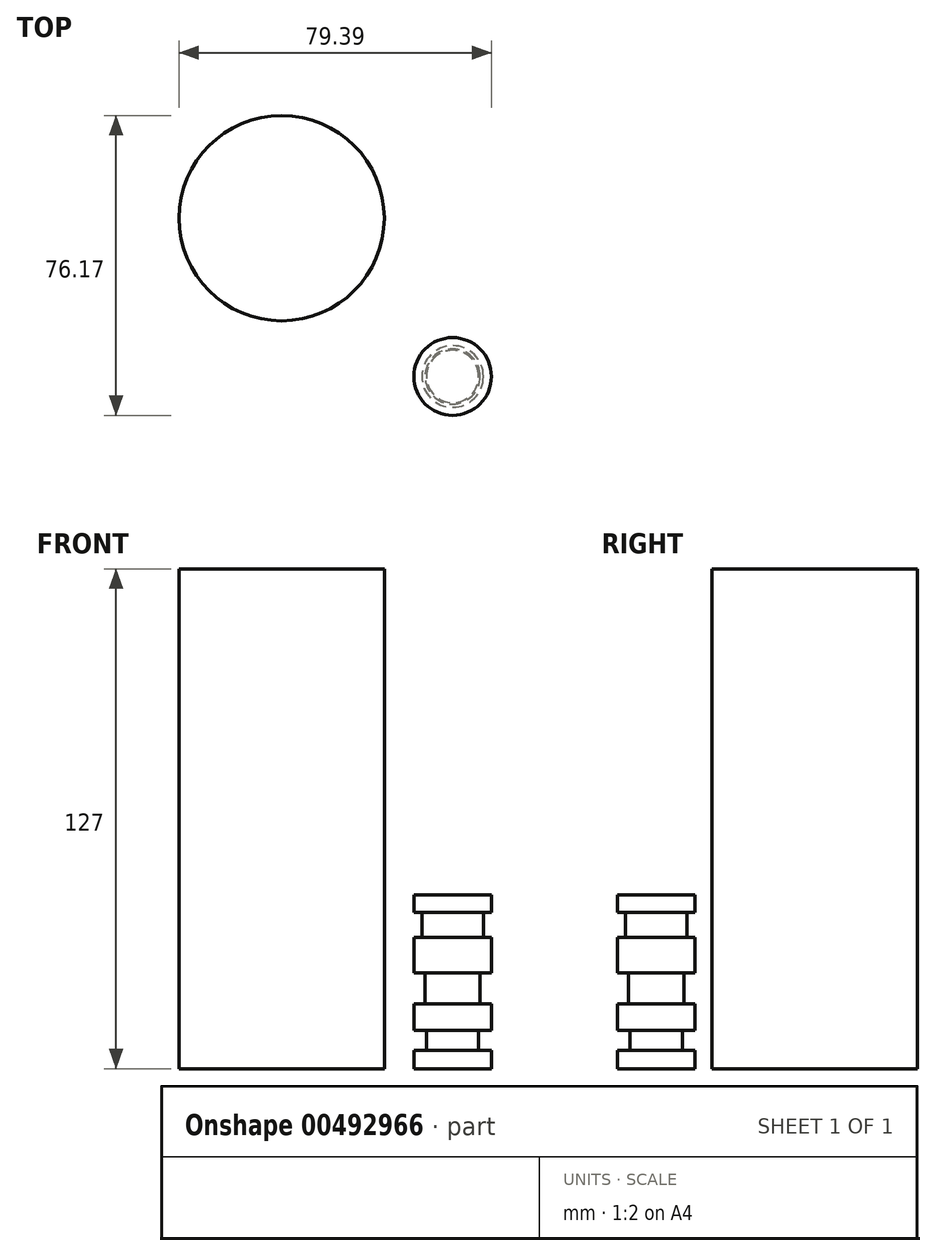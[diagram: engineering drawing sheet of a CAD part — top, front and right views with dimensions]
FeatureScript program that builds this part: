
annotation { "Feature Type Name" : "Feature", "Feature Type Description" : "" }
export const myFeature = defineFeature(function(context is Context, id is Id, definition is map)
    precondition{}
    {
        {
            var Q0;
            Q0=qCreatedBy(makeId("Top.planeOp"),FACE);
            var sketch = newSketch(context, id + "F0", { "sketchPlane" : qUnion([Q0])});
            skCircle(sketch, "E0", {"center": v(-43.44, 40.22) * mm, "radius": 26.09 * mm});
            skSolve(sketch);
        }
        {
            var Q0;
            Q0=makeQuery(id+"F0.imprint","IMPRINT",FACE,{"disambiguationData":[TD([[makeQuery(id+"F0.imprint","IMPRINT",EDGE,{"derivedFrom":sQuery(id+"F0.wireOp",EDGE,"E0")}),1.0]])]});
            extrude(context, id + "F1", {"entities" : qUnion([Q0]), "depth" : 127 * mm});
        }
        {
            var Q0;
            Q0=qCreatedBy(makeId("Right.planeOp"),FACE);
            var sketch = newSketch(context, id + "F2", { "sketchPlane" : qUnion([Q0])});
            skLineSegment(sketch, "E1.bottom", {"start": v(0, 0) * mm, "end": v(9.87, 0) * mm});
            skLineSegment(sketch, "E1.top", {"start": v(0, 44.13) * mm, "end": v(9.87, 44.13) * mm});
            skLineSegment(sketch, "E1.left", {"start": v(0, 0) * mm, "end": v(0, 44.13) * mm});
            skLineSegment(sketch, "E2.bottom", {"start": v(7.82, 39.66) * mm, "end": v(9.87, 39.66) * mm});
            skLineSegment(sketch, "E2.top", {"start": v(7.82, 33.3) * mm, "end": v(9.87, 33.3) * mm});
            skLineSegment(sketch, "E2.left", {"start": v(7.82, 39.66) * mm, "end": v(7.82, 33.3) * mm});
            skLineSegment(sketch, "E3.bottom", {"start": v(7, 24.36) * mm, "end": v(9.87, 24.36) * mm});
            skLineSegment(sketch, "E3.top", {"start": v(7, 16.47) * mm, "end": v(9.87, 16.47) * mm});
            skLineSegment(sketch, "E3.left", {"start": v(7, 24.36) * mm, "end": v(7, 16.47) * mm});
            skLineSegment(sketch, "E4.bottom", {"start": v(6.64, 9.77) * mm, "end": v(9.87, 9.77) * mm});
            skLineSegment(sketch, "E4.top", {"start": v(6.64, 4.59) * mm, "end": v(9.87, 4.59) * mm});
            skLineSegment(sketch, "E4.left", {"start": v(6.64, 9.77) * mm, "end": v(6.64, 4.59) * mm});
            skLineSegment(sketch, "E5.trimOffspring", {"start": v(9.87, 39.66) * mm, "end": v(9.87, 44.13) * mm});
            skLineSegment(sketch, "E6.trimOffspring", {"start": v(9.87, 24.36) * mm, "end": v(9.87, 33.3) * mm});
            skLineSegment(sketch, "E7.trimOffspring", {"start": v(9.87, 9.77) * mm, "end": v(9.87, 16.47) * mm});
            skLineSegment(sketch, "E8", {"start": v(9.87, 4.59) * mm, "end": v(9.87, 0) * mm});
            skSolve(sketch);
        }
        {
            var Q0;
            Q0=makeQuery(id+"F2.imprint","IMPRINT",FACE,{"disambiguationData":[TD([[makeQuery(id+"F2.imprint","IMPRINT",EDGE,{"derivedFrom":sQuery(id+"F2.wireOp",EDGE,"E1.bottom")}),1.0]])]});
            var Q1;
            Q1=sQuery(id+"F2.wireOp",EDGE,"E1.left");
            revolve(context, id + "F3", {"entities" : qUnion([Q0]), "axis" : qUnion([Q1]), "revolveType" : RevolveType.FULL});
        }
    });
